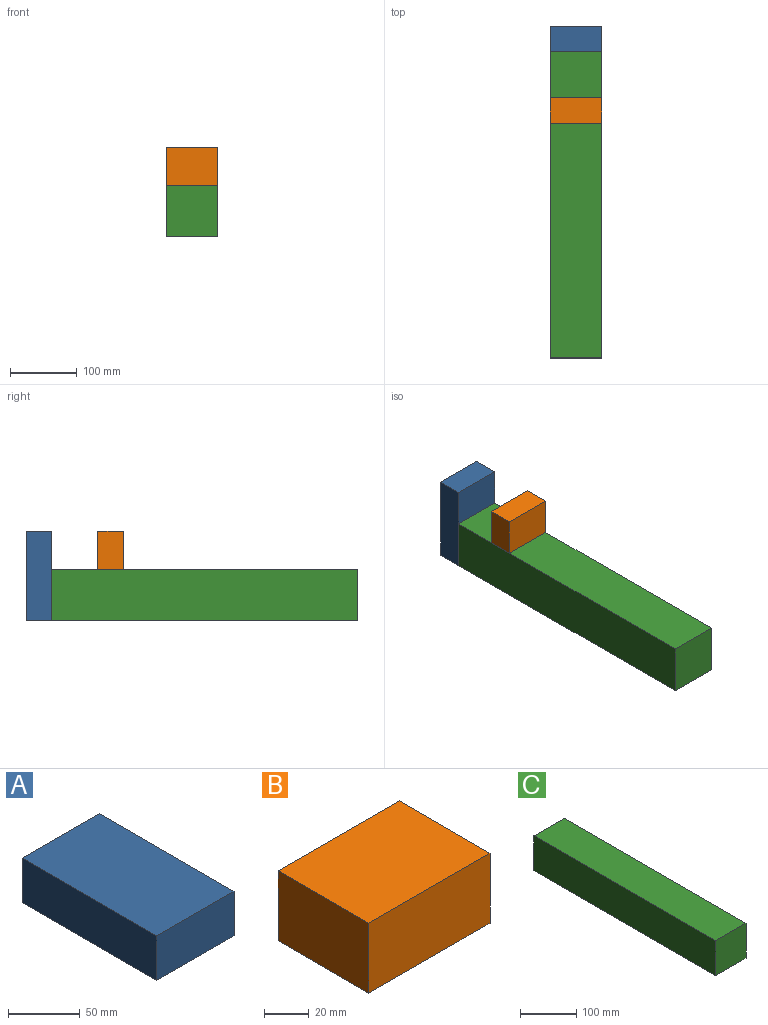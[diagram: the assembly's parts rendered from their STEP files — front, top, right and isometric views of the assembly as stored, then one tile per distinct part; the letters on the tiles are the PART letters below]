
ASSEMBLY  parts=3 mates=4
PART A: 6 faces, bbox 76.2x133.4x38.1 mm
  f0: plane 133.35x76.2mm, normal (0,0,1), area 10161.3mm2, adj f1,f3,f4,f5
  f1: plane 133.35x38.1mm, normal (-1,0,0), area 5080.6mm2, adj f0,f2,f4,f5
  f2: plane 133.35x76.2mm, normal (0,0,-1), area 10161.3mm2, adj f1,f3,f4,f5
  f3: plane 133.35x38.1mm, normal (1,0,0), area 5080.6mm2, adj f0,f2,f4,f5
  f4: plane 76.2x38.1mm, normal (0,-1,0), area 2903.2mm2, adj f0,f1,f2,f3
  f5: plane 76.2x38.1mm, normal (0,1,0), area 2903.2mm2, adj f0,f1,f2,f3
PART B: 6 faces, bbox 76.2x57.2x38.1 mm
  f0: plane 76.2x57.15mm, normal (0,0,1), area 4354.8mm2, adj f1,f3,f4,f5
  f1: plane 57.15x38.1mm, normal (-1,0,0), area 2177.4mm2, adj f0,f2,f4,f5
  f2: plane 76.2x57.15mm, normal (0,0,-1), area 4354.8mm2, adj f1,f3,f4,f5
  f3: plane 57.15x38.1mm, normal (1,0,0), area 2177.4mm2, adj f0,f2,f4,f5
  f4: plane 76.2x38.1mm, normal (0,-1,0), area 2903.2mm2, adj f0,f1,f2,f3
  f5: plane 76.2x38.1mm, normal (0,1,0), area 2903.2mm2, adj f0,f1,f2,f3
PART C: 6 faces, bbox 76.2x457.2x76.2 mm
  f0: plane 457.2x76.2mm, normal (0,0,1), area 34838.6mm2, adj f1,f3,f4,f5
  f1: plane 457.2x76.2mm, normal (-1,0,0), area 34838.6mm2, adj f0,f2,f4,f5
  f2: plane 457.2x76.2mm, normal (0,0,-1), area 34838.6mm2, adj f1,f3,f4,f5
  f3: plane 457.2x76.2mm, normal (1,0,0), area 34838.6mm2, adj f0,f2,f4,f5
  f4: plane 76.2x76.2mm, normal (0,-1,0), area 5806.4mm2, adj f0,f1,f2,f3
  f5: plane 76.2x76.2mm, normal (0,1,0), area 5806.4mm2, adj f0,f1,f2,f3
PLACE A rot(axis=(1,0,0),90deg) t=(-170.03,183.26,-3.36)mm
PLACE B rot(axis=(1,0,0),90deg) t=(-173.15,76.22,-3.36)mm
PLACE C t=(-170.03,145.16,-136.71)mm fixed
MATE planar A.f0 <-> C.f5  axis (0,-1,0) through (-131.93,145.16,-70.04)mm
MATE planar B.f4 <-> C.f0  axis (0,0,-1) through (-131.93,57.17,-60.51)mm
MATE planar B.f3 <-> C.f3  axis (1,0,0) through (-93.83,57.17,-31.94)mm
MATE planar A.f4 <-> C.f2  axis (0,0,-1) through (-131.93,164.21,-136.71)mm
